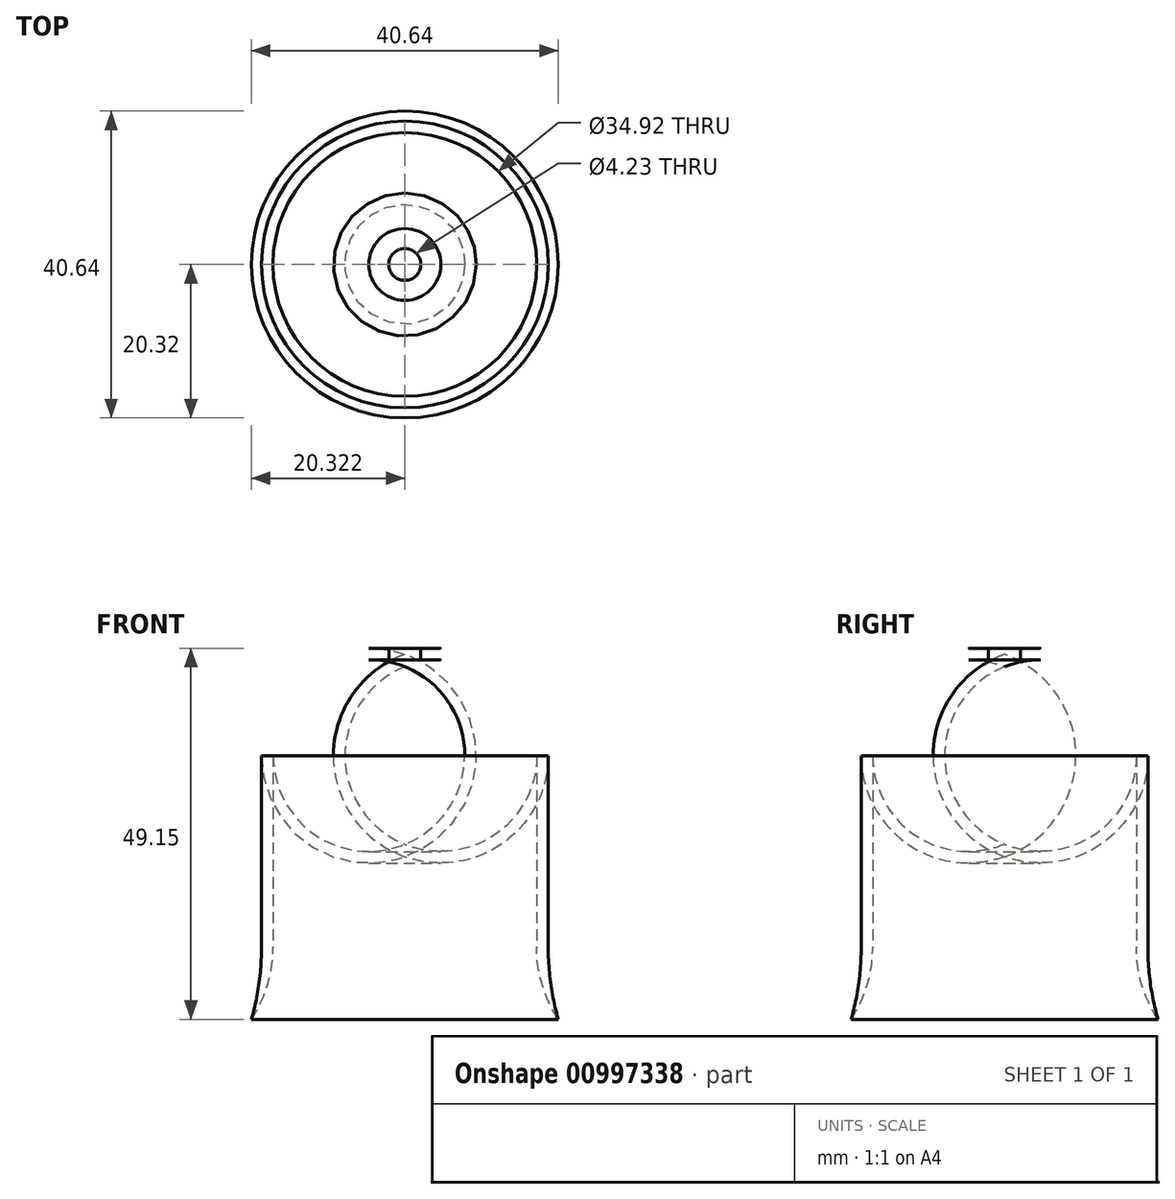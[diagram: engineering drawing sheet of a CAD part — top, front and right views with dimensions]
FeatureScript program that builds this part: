
annotation { "Feature Type Name" : "Feature", "Feature Type Description" : "" }
export const myFeature = defineFeature(function(context is Context, id is Id, definition is map)
    precondition{}
    {
        {
            var Q0;
            Q0=qCreatedBy(makeId("Front.planeOp"),FACE);
            var sketch = newSketch(context, id + "F0", { "sketchPlane" : qUnion([Q0])});
            skLineSegment(sketch, "E0", {"start": v(0, 0) * mm, "end": v(0, 25.4) * mm, "construction": true});
            skLineSegment(sketch, "E1", {"start": v(17.46, 38.1) * mm, "end": v(22.22, 38.1) * mm});
            skLineSegment(sketch, "E2", {"start": v(34.93, 25.4) * mm, "end": v(34.93, 0) * mm});
            skArc(sketch, "E3", {"start": v(12.7, 38.1) * mm, "mid": v(3.72, 34.38) * mm, "end": v(0, 25.4) * mm, "construction": true});
            skArc(sketch, "E4", {"start": v(34.93, 25.4) * mm, "mid": v(31.2, 34.38) * mm, "end": v(22.22, 38.1) * mm});
            skArc(sketch, "E5", {"start": v(-2.86, -9.53) * mm, "mid": v(-0.73, -4.97) * mm, "end": v(0, 0) * mm, "construction": true});
            skArc(sketch, "E6", {"start": v(34.92, 0) * mm, "mid": v(35.65, -4.97) * mm, "end": v(37.78, -9.52) * mm});
            skPoint(sketch, "E7", {"position": v(-2.86, -9.52) * mm});
            skPoint(sketch, "E8", {"position": v(37.78, -9.52) * mm});
            skLineSegment(sketch, "E9.0", {"start": v(36.45, 25.4) * mm, "end": v(36.45, 0) * mm});
            skLineSegment(sketch, "E9.1", {"start": v(-1.52, 0) * mm, "end": v(-1.52, 25.4) * mm, "construction": true});
            skArc(sketch, "E9.2", {"start": v(12.7, 39.62) * mm, "mid": v(2.64, 35.46) * mm, "end": v(-1.52, 25.4) * mm, "construction": true});
            skLineSegment(sketch, "E9.3", {"start": v(17.46, 39.62) * mm, "end": v(22.22, 39.62) * mm});
            skArc(sketch, "E9.4", {"start": v(36.45, 25.4) * mm, "mid": v(32.28, 35.46) * mm, "end": v(22.22, 39.62) * mm});
            skArc(sketch, "E10", {"start": v(-2.86, -9.53) * mm, "mid": v(-1.86, -4.8) * mm, "end": v(-1.52, 0) * mm, "construction": true});
            skArc(sketch, "E11", {"start": v(36.45, 0) * mm, "mid": v(36.78, -4.8) * mm, "end": v(37.78, -9.53) * mm});
            skLineSegment(sketch, "E12", {"start": v(17.46, 38.1) * mm, "end": v(17.46, 39.62) * mm});
            skSolve(sketch);
        }
        {
            var Q0;
            Q0=makeQuery(id+"F0.imprint","IMPRINT",FACE,{"disambiguationData":[TD([[makeQuery(id+"F0.imprint","IMPRINT",EDGE,{"derivedFrom":sQuery(id+"F0.wireOp",EDGE,"E1")}),1.0]])]});
            var Q1;
            Q1=sQuery(id+"F0.wireOp",EDGE,"E12");
            revolve(context, id + "F1", {"surfaceOperationType" : NewSurfaceOperationType.NEW, "entities" : qUnion([Q0]), "axis" : qUnion([Q1]), "revolveType" : RevolveType.FULL});
        }
        {
            var Q0;
            Q0=makeQuery(id+"F1.opRevolve","SWEPT_FACE",FACE,{"disambiguationData":[OSD([sQuery(id+"F0.wireOp",EDGE,"E9.3")])]});
            var sketch = newSketch(context, id + "F2", { "sketchPlane" : qUnion([Q0])});
            skCircle(sketch, "E13", {"center": v(17.46, 0) * mm, "radius": 2.12 * mm});
            skSolve(sketch);
        }
        {
            var Q0;
            Q0=makeQuery(id+"F2.imprint","IMPRINT",FACE,{"disambiguationData":[TD([[makeQuery(id+"F2.imprint","IMPRINT",EDGE,{"derivedFrom":sQuery(id+"F2.wireOp",EDGE,"E13")}),1.0]])]});
            extrude(context, id + "F3", {"entities" : qUnion([Q0]), "operationType" : NewBodyOperationType.REMOVE, "endBound" : BoundingType.UP_TO_NEXT, "oppositeDirection" : true, "depth" : 25.4 * mm, "offsetDistance" : 25.4 * mm});
        }
    });
